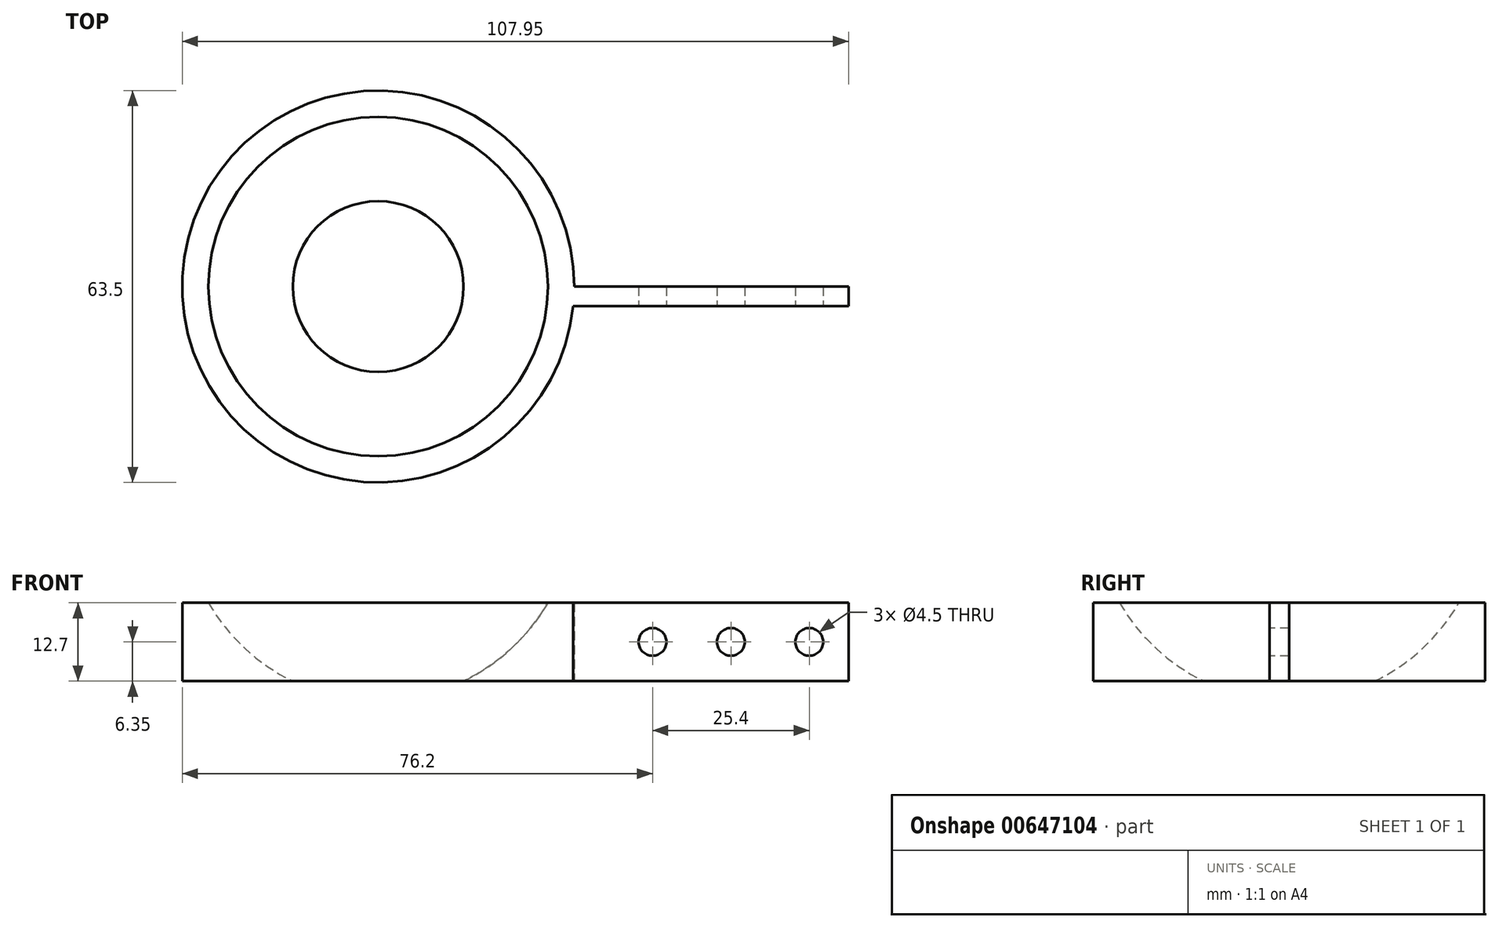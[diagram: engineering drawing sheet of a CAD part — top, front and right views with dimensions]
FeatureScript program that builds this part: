
annotation { "Feature Type Name" : "Feature", "Feature Type Description" : "" }
export const myFeature = defineFeature(function(context is Context, id is Id, definition is map)
    precondition{}
    {
        {
            var Q0;
            Q0=qCreatedBy(makeId("Top.planeOp"),FACE);
            var sketch = newSketch(context, id + "F0", { "sketchPlane" : qUnion([Q0])});
            skCircle(sketch, "E0", {"center": v(0, 0) * mm, "radius": 31.75 * mm});
            skSolve(sketch);
        }
        {
            var Q0;
            Q0=makeQuery(id+"F0.imprint","IMPRINT",FACE,{"disambiguationData":[TD([[makeQuery(id+"F0.imprint","IMPRINT",EDGE,{"derivedFrom":sQuery(id+"F0.wireOp",EDGE,"E0")}),1.0]])]});
            extrude(context, id + "F1", {"entities" : qUnion([Q0]), "depth" : 12.7 * mm, "offsetDistance" : 25.4 * mm});
        }
        {
            var Q0;
            Q0=qCreatedBy(makeId("Front.planeOp"),FACE);
            var sketch = newSketch(context, id + "F2", { "sketchPlane" : qUnion([Q0])});
            skCircle(sketch, "E1", {"center": v(0, 28.58) * mm, "radius": 31.75 * mm});
            skLineSegment(sketch, "E2", {"start": v(0, 60.33) * mm, "end": v(0, -3.17) * mm});
            skSolve(sketch);
        }
        {
            var Q0;
            {var subQ0=sQuery(id+"F2.wireOp",EDGE,"E2");Q0=makeQuery(id+"F2.imprint","IMPRINT",FACE,{"disambiguationData":[TD([[makeQuery(id+"F2.imprint","IMPRINT",EDGE,{"derivedFrom":subQ0}),1.0]])]});}
            var Q1;
            Q1=sQuery(id+"F2.wireOp",EDGE,"E2");
            revolve(context, id + "F3", {"operationType" : NewBodyOperationType.REMOVE, "entities" : qUnion([Q0]), "axis" : qUnion([Q1]), "revolveType" : RevolveType.FULL, "oppositeDirection" : true});
        }
        {
            var Q0;
            Q0=qCreatedBy(makeId("Right.planeOp"),FACE);
            cPlane(context, id + "F4", {"entities" : qUnion([Q0]), "cplaneType" : CPlaneType.OFFSET, "offset" : 76.2 * mm, "width" : 152.4 * mm, "height" : 152.4 * mm});
        }
        {
            var Q0;
            Q0=qCreatedBy(id+"F4.planeOp",FACE);
            var sketch = newSketch(context, id + "F5", { "sketchPlane" : qUnion([Q0])});
            skLineSegment(sketch, "E3.bottom", {"start": v(0, 0) * mm, "end": v(-3.17, 0) * mm});
            skLineSegment(sketch, "E3.top", {"start": v(0, 12.7) * mm, "end": v(-3.18, 12.7) * mm});
            skLineSegment(sketch, "E3.left", {"start": v(0, 0) * mm, "end": v(0, 12.7) * mm});
            skLineSegment(sketch, "E3.right", {"start": v(-3.18, 0) * mm, "end": v(-3.18, 12.7) * mm});
            skSolve(sketch);
        }
        {
            var Q0;
            Q0=makeQuery(id+"F5.imprint","IMPRINT",FACE,{"disambiguationData":[TD([[makeQuery(id+"F5.imprint","IMPRINT",EDGE,{"derivedFrom":sQuery(id+"F5.wireOp",EDGE,"E3.bottom")}),-1.0]])]});
            extrude(context, id + "F6", {"entities" : qUnion([Q0]), "operationType" : NewBodyOperationType.ADD, "endBound" : BoundingType.UP_TO_NEXT, "oppositeDirection" : true, "depth" : 25.4 * mm, "offsetDistance" : 25.4 * mm});
        }
        {
            var Q0;
            Q0=makeQuery(id+"F6.opExtrude","SWEPT_FACE",FACE,{"disambiguationData":[OSD([sQuery(id+"F5.wireOp",EDGE,"E3.right")])]});
            var sketch = newSketch(context, id + "F7", { "sketchPlane" : qUnion([Q0])});
            skPoint(sketch, "E4", {"position": v(44.45, 6.35) * mm});
            skPoint(sketch, "E5", {"position": v(69.85, 6.35) * mm});
            skPoint(sketch, "E6", {"position": v(57.15, 6.35) * mm});
            skPoint(sketch, "E6.positionSnap0", {"position": v(53.9, 12.7) * mm});
            skSolve(sketch);
        }
        {
            var Q0;
            Q0=sQuery(id+"F7.wireOp",VERTEX,"E4");
            var Q1;
            Q1=sQuery(id+"F7.wireOp",VERTEX,"E5");
            var Q2;
            Q2=sQuery(id+"F7.wireOp",VERTEX,"E6");
            var Q3;
            Q3=makeQuery(id+"F1.opExtrude","SWEPT_BODY",BODY,{"disambiguationData":[OSD([sQuery(id+"F0.wireOp",EDGE,"E0")])]});
            hole(context, id + "F8", {"style" : HoleStyle.SIMPLE, "endStyle" : HoleEndStyle.THROUGH, "standardTappedOrClearance" : lookupTablePath({ "standard" : "ANSI", "fit" : "Normal (ASME)", "size" : "#8", "type" : "Clearance" }), "standardBlindInLast" : lookupTablePath({ "fit" : "Free", "standard" : "ANSI", "size" : "#8", "type" : "Clearance" }), "holeDiameter" : 4.5 * mm, "majorDiameter" : 6.35 * mm, "isTappedThrough" : true, "tappedDepth" : 12.7 * mm, "tapClearance" : 3, "locations" : qUnion([Q0, Q1, Q2]), "scope" : qUnion([Q3])});
        }
    });
